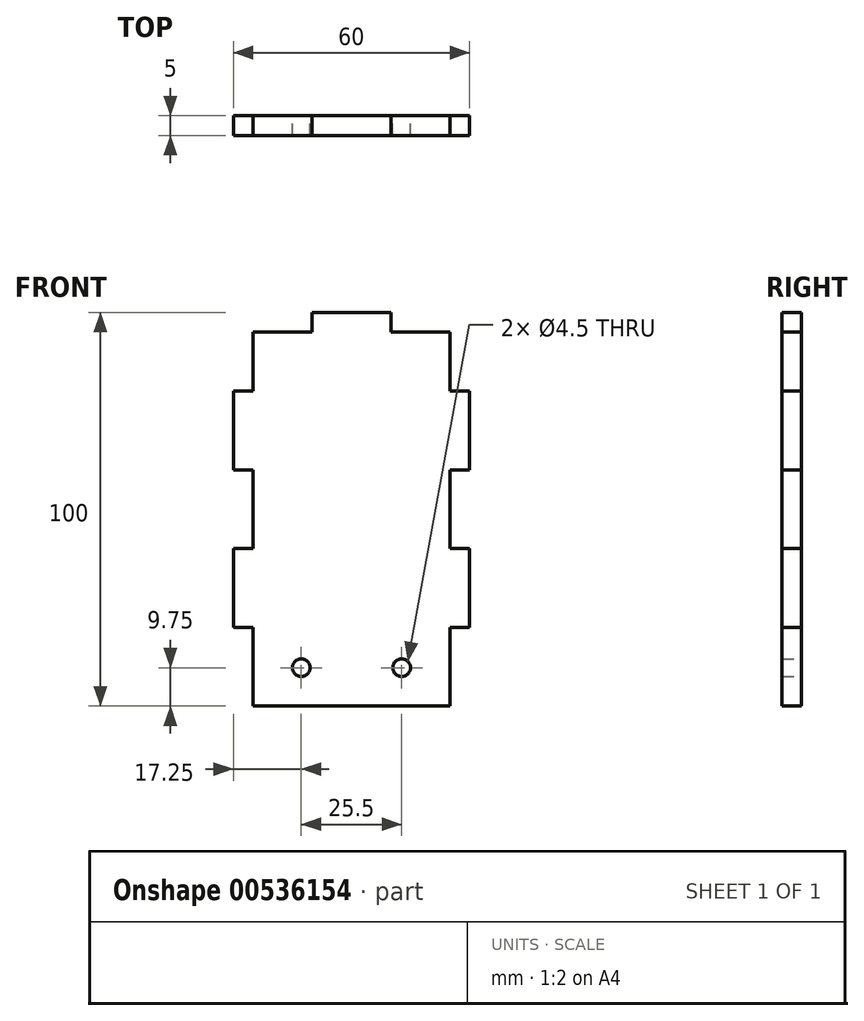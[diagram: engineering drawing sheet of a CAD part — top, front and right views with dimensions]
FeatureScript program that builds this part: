
annotation { "Feature Type Name" : "Feature", "Feature Type Description" : "" }
export const myFeature = defineFeature(function(context is Context, id is Id, definition is map)
    precondition{}
    {
        {
            var Q0;
            Q0=qCreatedBy(makeId("Front.planeOp"),FACE);
            var sketch = newSketch(context, id + "F0", { "sketchPlane" : qUnion([Q0])});
            skLineSegment(sketch, "E0.bottom", {"start": v(25, 47.5) * mm, "end": v(10, 47.5) * mm});
            skLineSegment(sketch, "E0.top", {"start": v(25, -47.5) * mm, "end": v(-25, -47.5) * mm});
            skLineSegment(sketch, "E0.left", {"start": v(25, 47.5) * mm, "end": v(25, 32.5) * mm});
            skLineSegment(sketch, "E0.right", {"start": v(-25, 47.5) * mm, "end": v(-25, 32.5) * mm});
            skPoint(sketch, "E0.middle", {"position": v(0, 0) * mm});
            skLineSegment(sketch, "E1", {"start": v(-30, -47.5) * mm, "end": v(-30, 52.5) * mm, "construction": true});
            skLineSegment(sketch, "E2", {"start": v(-30, 52.5) * mm, "end": v(30, 52.5) * mm, "construction": true});
            skLineSegment(sketch, "E3", {"start": v(30, 52.5) * mm, "end": v(30, -47.5) * mm, "construction": true});
            skLineSegment(sketch, "E4", {"start": v(25, -27.5) * mm, "end": v(30, -27.5) * mm});
            skLineSegment(sketch, "E5", {"start": v(30, -27.5) * mm, "end": v(30, -7.5) * mm});
            skLineSegment(sketch, "E6", {"start": v(30, -7.5) * mm, "end": v(25, -7.5) * mm});
            skLineSegment(sketch, "E7", {"start": v(25, 12.5) * mm, "end": v(30, 12.5) * mm});
            skLineSegment(sketch, "E8", {"start": v(30, 12.5) * mm, "end": v(30, 32.5) * mm});
            skLineSegment(sketch, "E9", {"start": v(30, 32.5) * mm, "end": v(25, 32.5) * mm});
            skLineSegment(sketch, "E10.trimOffspring", {"start": v(25, 12.5) * mm, "end": v(25, -7.5) * mm});
            skLineSegment(sketch, "E11.trimOffspring", {"start": v(25, -27.5) * mm, "end": v(25, -47.5) * mm});
            skLineSegment(sketch, "E12.MirrorCS", {"start": v(-30, 32.5) * mm, "end": v(-25, 32.5) * mm});
            skLineSegment(sketch, "E13.MirrorCS", {"start": v(-25, 12.5) * mm, "end": v(-30, 12.5) * mm});
            skLineSegment(sketch, "E14.MirrorCS", {"start": v(-30, -7.5) * mm, "end": v(-25, -7.5) * mm});
            skLineSegment(sketch, "E15.MirrorCS", {"start": v(-25, -27.5) * mm, "end": v(-30, -27.5) * mm});
            skLineSegment(sketch, "E16", {"start": v(-30, 32.5) * mm, "end": v(-30, 12.5) * mm});
            skLineSegment(sketch, "E17", {"start": v(-30, -7.5) * mm, "end": v(-30, -27.5) * mm});
            skLineSegment(sketch, "E18.trimOffspring", {"start": v(-25, 12.5) * mm, "end": v(-25, -7.5) * mm});
            skLineSegment(sketch, "E19.trimOffspring", {"start": v(-25, -27.5) * mm, "end": v(-25, -47.5) * mm});
            skLineSegment(sketch, "E20", {"start": v(-10, 47.5) * mm, "end": v(-10, 52.5) * mm});
            skLineSegment(sketch, "E21", {"start": v(-10, 52.5) * mm, "end": v(10, 52.5) * mm});
            skLineSegment(sketch, "E22", {"start": v(10, 52.5) * mm, "end": v(10, 47.5) * mm});
            skLineSegment(sketch, "E23.trimOffspring", {"start": v(-10, 47.5) * mm, "end": v(-25, 47.5) * mm});
            skLineSegment(sketch, "E24.bottom", {"start": v(-17.5, -61.5) * mm, "end": v(17.5, -61.5) * mm, "construction": true});
            skLineSegment(sketch, "E24.top", {"start": v(-17.5, -33.5) * mm, "end": v(17.5, -33.5) * mm, "construction": true});
            skLineSegment(sketch, "E24.left", {"start": v(-17.5, -61.5) * mm, "end": v(-17.5, -33.5) * mm, "construction": true});
            skLineSegment(sketch, "E24.right", {"start": v(17.5, -61.5) * mm, "end": v(17.5, -33.5) * mm, "construction": true});
            skPoint(sketch, "E24.middle", {"position": v(0, -47.5) * mm});
            skCircle(sketch, "E25", {"center": v(-12.75, -37.75) * mm, "radius": 2.25 * mm});
            skCircle(sketch, "E26", {"center": v(12.75, -37.75) * mm, "radius": 2.25 * mm});
            skSolve(sketch);
        }
        {
            var Q0;
            Q0 = qSketchRegion(id + "F0", true);
            extrude(context, id + "F1", {"entities" : qUnion([Q0]), "depth" : 5 * mm, "offsetDistance" : 25 * mm});
        }
    });
